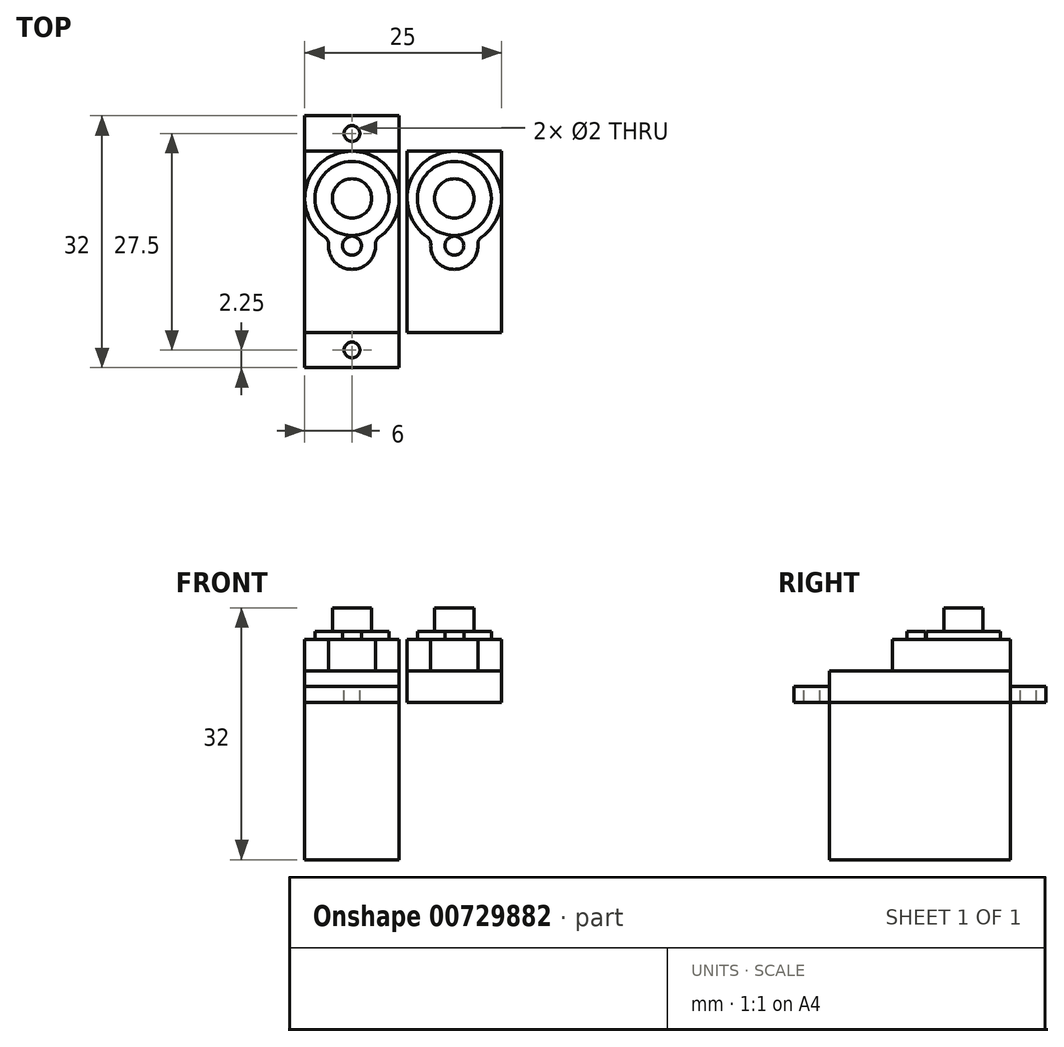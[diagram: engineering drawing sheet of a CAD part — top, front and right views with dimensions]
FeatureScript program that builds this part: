
annotation { "Feature Type Name" : "Feature", "Feature Type Description" : "" }
export const myFeature = defineFeature(function(context is Context, id is Id, definition is map)
    precondition{}
    {
        {
            var Q0;
            Q0=qCreatedBy(makeId("Top.planeOp"),FACE);
            var sketch = newSketch(context, id + "F0", { "sketchPlane" : qUnion([Q0])});
            skLineSegment(sketch, "E0.bottom", {"start": v(0, 0) * mm, "end": v(12, 0) * mm});
            skLineSegment(sketch, "E0.top", {"start": v(0, 23) * mm, "end": v(12, 23) * mm});
            skLineSegment(sketch, "E0.left", {"start": v(0, 0) * mm, "end": v(0, 23) * mm});
            skLineSegment(sketch, "E0.right", {"start": v(12, 0) * mm, "end": v(12, 23) * mm});
            skSolve(sketch);
        }
        {
            var Q0;
            Q0=makeQuery(id+"F0.imprint","IMPRINT",FACE,{"disambiguationData":[TD([[makeQuery(id+"F0.imprint","IMPRINT",EDGE,{"derivedFrom":sQuery(id+"F0.wireOp",EDGE,"E0.bottom")}),1.0]])]});
            extrude(context, id + "F1", {"entities" : qUnion([Q0]), "depth" : 20 * mm, "offsetDistance" : 25 * mm});
        }
        {
            var Q0;
            Q0=makeQuery(id+"F1.opExtrude","CAP_FACE",FACE,{"disambiguationData":[OSD([sQuery(id+"F0.wireOp",EDGE,"E0.bottom"),sQuery(id+"F0.wireOp",EDGE,"E0.top"),sQuery(id+"F0.wireOp",EDGE,"E0.left"),sQuery(id+"F0.wireOp",EDGE,"E0.right")])],"isStart":false});
            var sketch = newSketch(context, id + "F2", { "sketchPlane" : qUnion([Q0])});
            skLineSegment(sketch, "E1", {"start": v(12, 27.5) * mm, "end": v(0, 27.5) * mm});
            skLineSegment(sketch, "E2", {"start": v(0, 27.5) * mm, "end": v(0, -4.5) * mm});
            skLineSegment(sketch, "E3", {"start": v(0, -4.5) * mm, "end": v(12, -4.5) * mm});
            skLineSegment(sketch, "E4", {"start": v(12, 27.5) * mm, "end": v(12, -4.5) * mm});
            skSolve(sketch);
        }
        {
            var Q0;
            {var subQ2=sQuery(id+"F2.wireOp",EDGE,"E3");Q0=makeQuery(id+"F2.imprint","IMPRINT",FACE,{"disambiguationData":[TD([[makeQuery(id+"F2.imprint","IMPRINT",EDGE,{"derivedFrom":subQ2}),1.0]])]});}
            var Q1;
            {var subQ0=sQuery(id+"F2.wireOp",EDGE,"E1");Q1=makeQuery(id+"F2.imprint","IMPRINT",FACE,{"disambiguationData":[TD([[makeQuery(id+"F2.imprint","IMPRINT",EDGE,{"derivedFrom":subQ0}),1.0]])]});}
            extrude(context, id + "F3", {"entities" : qUnion([Q0, Q1]), "depth" : 2 * mm, "offsetDistance" : 25 * mm});
        }
        {
            var Q0;
            Q0=makeQuery(id+"F1.opExtrude","CAP_FACE",FACE,{"disambiguationData":[OSD([sQuery(id+"F0.wireOp",EDGE,"E0.bottom"),sQuery(id+"F0.wireOp",EDGE,"E0.top"),sQuery(id+"F0.wireOp",EDGE,"E0.left"),sQuery(id+"F0.wireOp",EDGE,"E0.right")])],"isStart":false});
            extrude(context, id + "F4", {"entities" : qUnion([Q0]), "depth" : 4 * mm, "offsetDistance" : 25 * mm});
        }
        {
            var Q0;
            Q0=makeQuery(id+"F4.opExtrude","CAP_FACE",FACE,{"disambiguationData":[OSD([sQuery(id+"F0.wireOp",EDGE,"E0.bottom"),sQuery(id+"F0.wireOp",EDGE,"E0.top"),sQuery(id+"F0.wireOp",EDGE,"E0.left"),sQuery(id+"F0.wireOp",EDGE,"E0.right")])],"isStart":false});
            var sketch = newSketch(context, id + "F5", { "sketchPlane" : qUnion([Q0])});
            skArc(sketch, "E5", {"start": v(9.42, 12.07) * mm, "mid": v(6, 23) * mm, "end": v(2.58, 12.07) * mm});
            skPoint(sketch, "E5.centerSnap0", {"position": v(6, 23) * mm});
            skArc(sketch, "E6", {"start": v(3, 11.19) * mm, "mid": v(6, 8) * mm, "end": v(9, 11.19) * mm});
            skPoint(sketch, "E7.visualSharp", {"position": v(3.1, 11.75) * mm});
            skArc(sketch, "E7.filletArc", {"start": v(3, 11.19) * mm, "mid": v(2.9, 11.69) * mm, "end": v(2.58, 12.07) * mm});
            skPoint(sketch, "E8.visualSharp", {"position": v(8.9, 11.75) * mm});
            skArc(sketch, "E8.filletArc", {"start": v(9.42, 12.07) * mm, "mid": v(9.1, 11.69) * mm, "end": v(9, 11.19) * mm});
            skSolve(sketch);
        }
        {
            var Q0;
            Q0=makeQuery(id+"F5.imprint","IMPRINT",FACE,{"disambiguationData":[TD([[makeQuery(id+"F5.imprint","IMPRINT",EDGE,{"derivedFrom":sQuery(id+"F5.wireOp",EDGE,"E6")}),1.0]])]});
            extrude(context, id + "F6", {"entities" : qUnion([Q0]), "operationType" : NewBodyOperationType.ADD, "depth" : 4 * mm, "offsetDistance" : 25 * mm});
        }
        {
            var Q0;
            Q0=makeQuery(id+"F6.opExtrude","CAP_FACE",FACE,{"disambiguationData":[OSD([sQuery(id+"F5.wireOp",EDGE,"E5"),sQuery(id+"F5.wireOp",EDGE,"E6"),sQuery(id+"F5.wireOp",EDGE,"E7.filletArc"),sQuery(id+"F5.wireOp",EDGE,"E8.filletArc")])],"isStart":false});
            var sketch = newSketch(context, id + "F7", { "sketchPlane" : qUnion([Q0])});
            skCircle(sketch, "E9", {"center": v(6, 11) * mm, "radius": 1.2 * mm});
            skCircle(sketch, "E10", {"center": v(6, 17) * mm, "radius": 4.7 * mm});
            skSolve(sketch);
        }
        {
            var Q0;
            Q0=makeQuery(id+"F7.imprint","IMPRINT",FACE,{"disambiguationData":[TD([[makeQuery(id+"F7.imprint","IMPRINT",EDGE,{"derivedFrom":sQuery(id+"F7.wireOp",EDGE,"E10")}),1.0]])]});
            var Q1;
            Q1=makeQuery(id+"F7.imprint","IMPRINT",FACE,{"disambiguationData":[TD([[makeQuery(id+"F7.imprint","IMPRINT",EDGE,{"derivedFrom":sQuery(id+"F7.wireOp",EDGE,"E9")}),1.0]])]});
            extrude(context, id + "F8", {"entities" : qUnion([Q0, Q1]), "operationType" : NewBodyOperationType.ADD, "depth" : 1 * mm, "offsetDistance" : 25 * mm});
        }
        {
            var Q0;
            Q0=makeQuery(id+"F3.opExtrude","CAP_FACE",FACE,{"disambiguationData":[OSD([sQuery(id+"F0.wireOp",EDGE,"E0.bottom"),sQuery(id+"F2.wireOp",EDGE,"E2"),sQuery(id+"F2.wireOp",EDGE,"E3"),sQuery(id+"F2.wireOp",EDGE,"E4")])],"isStart":false});
            var sketch = newSketch(context, id + "F9", { "sketchPlane" : qUnion([Q0])});
            skCircle(sketch, "E11", {"center": v(6, -2.25) * mm, "radius": 1 * mm});
            skPoint(sketch, "E11.centerSnap0", {"position": v(6, -4.5) * mm});
            skPoint(sketch, "E11.centerSnap1", {"position": v(0, -2.25) * mm});
            skSolve(sketch);
        }
        {
            var Q0;
            Q0=makeQuery(id+"F3.opExtrude","CAP_FACE",FACE,{"disambiguationData":[OSD([sQuery(id+"F0.wireOp",EDGE,"E0.top"),sQuery(id+"F2.wireOp",EDGE,"E1"),sQuery(id+"F2.wireOp",EDGE,"E2"),sQuery(id+"F2.wireOp",EDGE,"E4")])],"isStart":false});
            var sketch = newSketch(context, id + "F10", { "sketchPlane" : qUnion([Q0])});
            skCircle(sketch, "E12", {"center": v(6, 25.25) * mm, "radius": 1 * mm});
            skPoint(sketch, "E12.centerSnap0", {"position": v(6, 27.5) * mm});
            skPoint(sketch, "E12.centerSnap1", {"position": v(12, 25.25) * mm});
            skSolve(sketch);
        }
        {
            var Q0;
            Q0=makeQuery(id+"F9.imprint","IMPRINT",FACE,{"disambiguationData":[TD([[makeQuery(id+"F9.imprint","IMPRINT",EDGE,{"derivedFrom":sQuery(id+"F9.wireOp",EDGE,"E11")}),1.0]])]});
            var Q1;
            Q1=makeQuery(id+"F10.imprint","IMPRINT",FACE,{"disambiguationData":[TD([[makeQuery(id+"F10.imprint","IMPRINT",EDGE,{"derivedFrom":sQuery(id+"F10.wireOp",EDGE,"E12")}),1.0]])]});
            extrude(context, id + "F11", {"entities" : qUnion([Q0, Q1]), "operationType" : NewBodyOperationType.REMOVE, "endBound" : BoundingType.THROUGH_ALL, "oppositeDirection" : true, "depth" : 25 * mm, "offsetDistance" : 25 * mm});
        }
        {
            var Q0;
            Q0=makeQuery(id+"F8.opExtrude","CAP_FACE",FACE,{"disambiguationData":[OSD([sQuery(id+"F7.wireOp",EDGE,"E10")])],"isStart":false});
            var sketch = newSketch(context, id + "F12", { "sketchPlane" : qUnion([Q0])});
            skCircle(sketch, "E13", {"center": v(6, 17) * mm, "radius": 2.5 * mm});
            skSolve(sketch);
        }
        {
            var Q0;
            Q0=makeQuery(id+"F12.imprint","IMPRINT",FACE,{"disambiguationData":[TD([[makeQuery(id+"F12.imprint","IMPRINT",EDGE,{"derivedFrom":sQuery(id+"F12.wireOp",EDGE,"E13")}),1.0]])]});
            extrude(context, id + "F13", {"entities" : qUnion([Q0]), "operationType" : NewBodyOperationType.ADD, "depth" : 3 * mm, "offsetDistance" : 25 * mm});
        }
        {
            var Q0;
            Q0=makeQuery(id+"F4.opExtrude","SWEPT_BODY",BODY,{"disambiguationData":[OSD([sQuery(id+"F0.wireOp",EDGE,"E0.bottom"),sQuery(id+"F0.wireOp",EDGE,"E0.top"),sQuery(id+"F0.wireOp",EDGE,"E0.left"),sQuery(id+"F0.wireOp",EDGE,"E0.right")])]});
            transform(context, id + "F14", {"entities" : qUnion([Q0]), "transformType" : TransformType.TRANSLATION_3D, "dx" : 13 * mm, "dy" : 0 * mm, "dz" : 0 * mm, "makeCopy" : true});
        }
    });
